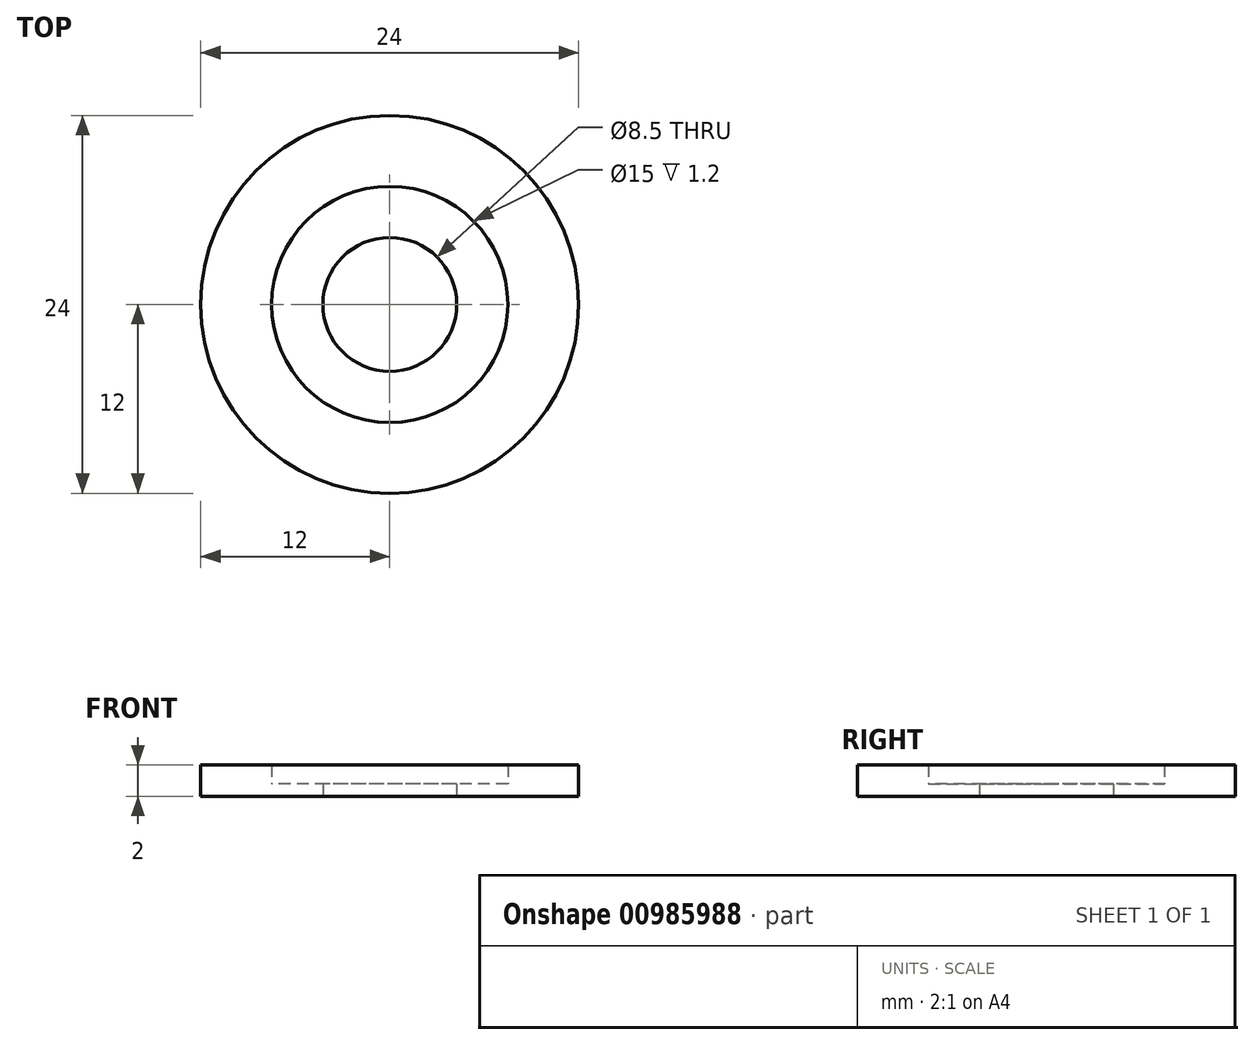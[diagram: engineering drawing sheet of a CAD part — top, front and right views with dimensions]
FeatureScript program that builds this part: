
annotation { "Feature Type Name" : "Feature", "Feature Type Description" : "" }
export const myFeature = defineFeature(function(context is Context, id is Id, definition is map)
    precondition{}
    {
        {
            var Q0;
            Q0=qCreatedBy(makeId("Top.planeOp"),FACE);
            var sketch = newSketch(context, id + "F0", { "sketchPlane" : qUnion([Q0])});
            skCircle(sketch, "E0", {"center": v(0, 0) * mm, "radius": 4.25 * mm});
            skCircle(sketch, "E1", {"center": v(0, 0) * mm, "radius": 7.5 * mm});
            skCircle(sketch, "E2", {"center": v(0, 0) * mm, "radius": 12 * mm});
            skSolve(sketch);
        }
        {
            var Q0;
            Q0=makeQuery(id+"F0.imprint","IMPRINT",FACE,{"disambiguationData":[TD([[makeQuery(id+"F0.imprint","IMPRINT",EDGE,{"derivedFrom":sQuery(id+"F0.wireOp",EDGE,"E0")}),-1.0]])]});
            extrude(context, id + "F1", {"entities" : qUnion([Q0]), "depth" : .8 * mm, "offsetDistance" : 25 * mm});
        }
        {
            var Q0;
            Q0=makeQuery(id+"F0.imprint","IMPRINT",FACE,{"disambiguationData":[TD([[makeQuery(id+"F0.imprint","IMPRINT",EDGE,{"derivedFrom":sQuery(id+"F0.wireOp",EDGE,"E1")}),-1.0]])]});
            extrude(context, id + "F2", {"entities" : qUnion([Q0]), "operationType" : NewBodyOperationType.ADD, "depth" : 2 * mm, "offsetDistance" : 25 * mm});
        }
    });
